# Revit family: SH-1398
name_source: partatom
category: Lighting Fixtures
revit_build: Autodesk Revit 2017 (Build: 20160225_1515(x64)
units: mm (PartAtom-declared; Revit-internal decimal feet)

## family parameters
Always vertical = No
Cut with Voids When Loaded = No
Light Source = No
OmniClass Number = 23.80.70.00
OmniClass Title = Lighting
Part Type = Normal
Room Calculation Point = No
Round Connector Dimension = Use Diameter
Shared = Yes
Work Plane-Based = Yes

## types (3) — shared parameters
Body Material = Aluminum
Body color = White color1
Default Elevation = 121.9 cm
Diameter = 5.6 cm
Diffuser = light
Flicker = Free Flicker
Height = 11.1 cm
IP = IP65
Lamp = LED
Manufacturer = SHOA
Model = SH-1398-Jetlight
Protection Class = Class I
Type medule = Power LED
URL = https://www.shoaco.com
Voltage/Frequency = 230V/50HZ
Website = www.shoaco.com
color rendering index(CRI) = 80<
consumption current = 0 A
wattage = 3 W

## per-type parameters (varying)
| type | 2000K | 3000K | 6500K | color temperature |
| Sh-1398-Jetlight(White color-2000K-LED) | Yes | No | No | 2000K |
| Sh-1398-Jetlight(White color-3000K-LED) | No | Yes | No | 3000K |
| Sh-1398-Jetlight(White color-6500K-LED) | No | No | Yes | 6500K |

## geometry (parser evidence)
native form markers: Sweep x9
no freeform markers — native parametric forms only
